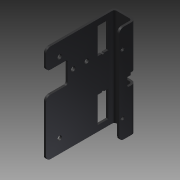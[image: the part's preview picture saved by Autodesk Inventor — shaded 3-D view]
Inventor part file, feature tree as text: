
AUTODESK INVENTOR PART (.ipt)
format: ipt  version: 2015 (Build 190159000, 159)  size: 406,528 bytes
history: native  units: mm
features: extrude x9, other x2, fillet x1, hole x1, plane x1, projected_geometry x1, imported_body x1
ambient origin geometry x8: Origin, YZ Plane, XZ Plane, XY Plane, X Axis, Y Axis, Z Axis, Center Point
bodies: Solid1 (feature_tree)
feature tree (16):
  other  "C04H030031-x-end-motor.ipt"
  extrude  "Extrusión1"  Depth=10.0mm
  extrude  "Extrusión6"  Depth=10.0mm TaperAngle=0.0deg
  extrude  "Extrusión11"  Depth=10.0mm TaperAngle=0.0deg
  extrude  "Extrusión12"  Depth=10.0mm TaperAngle=0.0deg
  extrude  "Extrusión17"  Depth=2.0mm TaperAngle=0.0deg
  fillet  "Redondeo de esquina4"  Radius=2.0mm
  extrude  "Extrusión18"  Depth=18.0mm
  hole  "Agujero2"  [1 undecoded]
  extrude  "Extrusión13"  Depth=15.7mm
  plane  "Plano de trabajo1"
  extrude  "Extrusión14"  Depth=2.0mm TaperAngle=0.0deg
  extrude  "Extrusión16"  Depth=2.0mm
  projected_geometry  "Contorno proyectado1"
  imported_body  "DerivedBody::C04H030031-x-end-motor.ipt"
  other  "Definición1"
note: 1 required parameter value undecoded (feature->parameter linkage not recoverable at this tier; creation-order binding heuristic only, values carry confidence <= 0.55)
